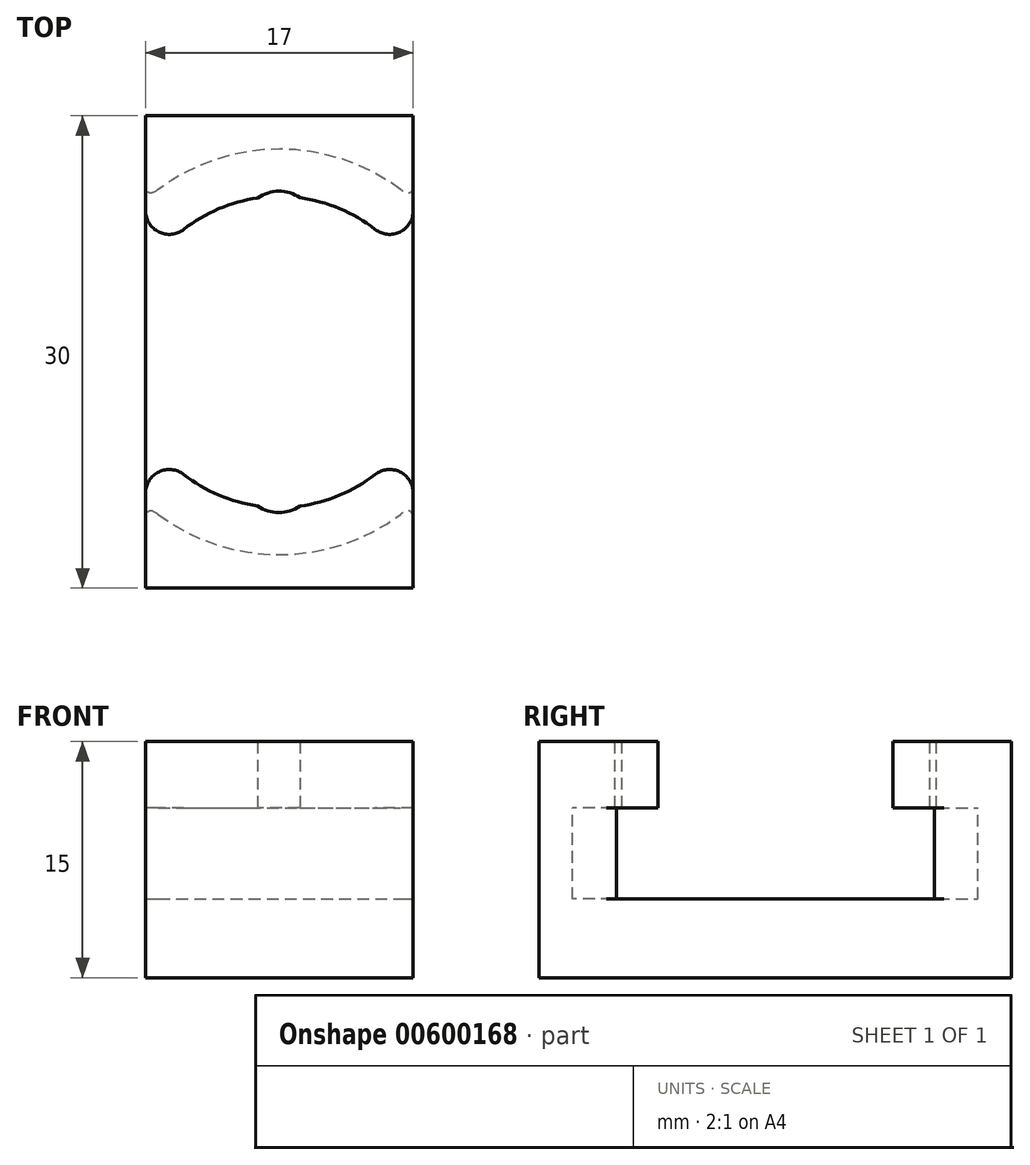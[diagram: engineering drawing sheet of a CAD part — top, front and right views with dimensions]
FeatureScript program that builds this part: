
annotation { "Feature Type Name" : "Feature", "Feature Type Description" : "" }
export const myFeature = defineFeature(function(context is Context, id is Id, definition is map)
    precondition{}
    {
        {
            var Q0;
            Q0=qCreatedBy(makeId("Top.planeOp"),FACE);
            var sketch = newSketch(context, id + "F0", { "sketchPlane" : qUnion([Q0])});
            skCircle(sketch, "E0", {"center": v(0, 0) * mm, "radius": 12.88 * mm});
            skSolve(sketch);
        }
        {
            var Q0;
            Q0=qSketchRegion(id+"F0",true);
            extrude(context, id + "F1", {"entities" : qUnion([Q0]), "oppositeDirection" : true, "depth" : 5.8 * mm, "offsetDistance" : 25 * mm});
        }
        {
            var Q0;
            Q0=qCreatedBy(makeId("Top.planeOp"),FACE);
            var sketch = newSketch(context, id + "F2", { "sketchPlane" : qUnion([Q0])});
            skCircle(sketch, "E1", {"center": v(0, 0) * mm, "radius": 9.88 * mm});
            skSolve(sketch);
        }
        {
            var Q0;
            Q0=qSketchRegion(id+"F2",true);
            extrude(context, id + "F3", {"entities" : qUnion([Q0]), "operationType" : NewBodyOperationType.ADD, "depth" : 12 * mm, "offsetDistance" : 25 * mm});
        }
        {
            var Q0;
            Q0=qCreatedBy(makeId("Top.planeOp"),FACE);
            var sketch = newSketch(context, id + "F4", { "sketchPlane" : qUnion([Q0])});
            skArc(sketch, "E2", {"start": v(1.01, 8.93) * mm, "mid": v(1, 8.94) * mm, "end": v(1, 8.95) * mm});
            skPoint(sketch, "E3.orphan", {"position": v(0, 9.05) * mm});
            skArc(sketch, "E4", {"start": v(2.13, 8.75) * mm, "mid": v(-0.03, 10.2) * mm, "end": v(-2.2, 8.75) * mm});
            skArc(sketch, "E5", {"start": v(-2.2, 8.75) * mm, "mid": v(-0.03, 9.02) * mm, "end": v(2.13, 8.76) * mm});
            skSolve(sketch);
        }
        {
            var Q0;
            Q0=qSketchRegion(id+"F4",true);
            extrude(context, id + "F5", {"entities" : qUnion([Q0]), "depth" : 5 * mm, "offsetDistance" : 25 * mm});
        }
        {
            var Q0;
            Q0=makeQuery(id+"F5.opExtrude","SWEPT_BODY",BODY,{"disambiguationData":[OSD([sQuery(id+"F4.wireOp",EDGE,"E4"),sQuery(id+"F4.wireOp",EDGE,"E5")])]});
            var Q1;
            Q1=qCreatedBy(makeId("Front.planeOp"),FACE);
            mirror(context, id + "F6", {"entities" : qUnion([Q0]), "mirrorPlane" : qUnion([Q1])});
        }
        {
            var Q0;
            Q0=qCreatedBy(makeId("Top.planeOp"),FACE);
            var sketch = newSketch(context, id + "F7", { "sketchPlane" : qUnion([Q0])});
            skLineSegment(sketch, "E6.bottom", {"start": v(-9, -13.5) * mm, "end": v(9, -13.5) * mm});
            skLineSegment(sketch, "E6.top", {"start": v(-9, 13.5) * mm, "end": v(9, 13.5) * mm});
            skLineSegment(sketch, "E6.left", {"start": v(-9, -13.5) * mm, "end": v(-9, 13.5) * mm});
            skLineSegment(sketch, "E6.right", {"start": v(9, -13.5) * mm, "end": v(9, 13.5) * mm});
            skPoint(sketch, "E6.middle", {"position": v(0, 0) * mm});
            skLineSegment(sketch, "E7.bottom", {"start": v(-15, -15) * mm, "end": v(15, -15) * mm});
            skLineSegment(sketch, "E7.top", {"start": v(-15, 15) * mm, "end": v(15, 15) * mm});
            skLineSegment(sketch, "E7.left", {"start": v(-15, -15) * mm, "end": v(-15, 15) * mm});
            skLineSegment(sketch, "E7.right", {"start": v(15, -15) * mm, "end": v(15, 15) * mm});
            skSolve(sketch);
        }
        {
            var Q0;
            Q0=qSketchRegion(id+"F7",true);
            extrude(context, id + "F8", {"entities" : qUnion([Q0]), "endBound" : BoundingType.SYMMETRIC, "depth" : 20 * mm, "offsetDistance" : 25 * mm});
        }
        {
            var Q0;
            Q0=makeQuery(id+"F8.opExtrude","SWEPT_BODY",BODY,{"disambiguationData":[OSD([sQuery(id+"F7.wireOp",EDGE,"E6.bottom"),sQuery(id+"F7.wireOp",EDGE,"E6.top"),sQuery(id+"F7.wireOp",EDGE,"E6.left"),sQuery(id+"F7.wireOp",EDGE,"E6.right"),sQuery(id+"F7.wireOp",EDGE,"E7.bottom"),sQuery(id+"F7.wireOp",EDGE,"E7.top"),sQuery(id+"F7.wireOp",EDGE,"E7.left"),sQuery(id+"F7.wireOp",EDGE,"E7.right")])]});
            var Q1;
            Q1=makeQuery(id+"F1.opExtrude","SWEPT_BODY",BODY,{"disambiguationData":[OSD([sQuery(id+"F0.wireOp",EDGE,"E0")])]});
            booleanBodies(context, id + "F9", {"operationType" : BooleanOperationType.SUBTRACTION, "tools" : qUnion([Q0]), "targets" : qUnion([Q1])});
        }
        {
            var Q0;
            Q0=qCreatedBy(makeId("Front.planeOp"),FACE);
            cPlane(context, id + "F11", {"entities" : qUnion([Q0]), "cplaneType" : CPlaneType.OFFSET, "offset" : 0 * mm, "width" : 150 * mm, "height" : 150 * mm});
        }
        {
            var Q0;
            Q0=qCreatedBy(id+"F11.planeOp",FACE);
            var sketch = newSketch(context, id + "F12", { "sketchPlane" : qUnion([Q0])});
            skLineSegment(sketch, "E8", {"start": v(0, 21.17) * mm, "end": v(0, -19.55) * mm});
            skSolve(sketch);
        }
        {
            var Q0;
            Q0=makeQuery(id+"F10.boolean.opBoolean","MERGE",FACE,{"derivedFrom":[makeQuery(id+"F1.opExtrude","CAP_FACE",FACE,{"disambiguationData":[OSD([sQuery(id+"F0.wireOp",EDGE,"E0")])],"isStart":false}),makeQuery(id+"F10.opExtrude","CAP_FACE",FACE,{"disambiguationData":[OSD([sQuery(id+"FGjzGYSQMg9Bp05_83.wireOp",EDGE,"KViSTKkF-VcMX-bRgI-X5AM-c6BNTwQ1Txp8"),sQuery(id+"FGjzGYSQMg9Bp05_83.wireOp",EDGE,"hnSNV8Ac-OkOP-zyx9-2yCD-nNF2xH7uDtxq"),sQuery(id+"FGjzGYSQMg9Bp05_83.wireOp",EDGE,"YhqCyHHE-mmT6-Zo3s-CP1x-K7R7TVIkhwK0"),sQuery(id+"FGjzGYSQMg9Bp05_83.wireOp",EDGE,"bfDPCBwk-4LN5-2Otn-u8De-q76RYstfvR2Y")])],"isStart":true})]});
            cPlane(context, id + "F14", {"entities" : qUnion([Q0]), "cplaneType" : CPlaneType.OFFSET, "offset" : 5 * mm, "width" : 150 * mm, "height" : 150 * mm});
        }
        {
            var Q0;
            Q0=qCreatedBy(id+"F14.planeOp",FACE);
            var sketch = newSketch(context, id + "F15", { "sketchPlane" : qUnion([Q0])});
            skLineSegment(sketch, "E9.bottom", {"start": v(-8.5, 15) * mm, "end": v(8.5, 15) * mm});
            skLineSegment(sketch, "E9.top", {"start": v(-8.5, -15) * mm, "end": v(8.5, -15) * mm});
            skLineSegment(sketch, "E9.left", {"start": v(-8.5, 15) * mm, "end": v(-8.5, -15) * mm});
            skLineSegment(sketch, "E9.right", {"start": v(8.5, 15) * mm, "end": v(8.5, -15) * mm});
            skPoint(sketch, "E9.middle", {"position": v(0, 0) * mm});
            skSolve(sketch);
        }
        {
            var Q0;
            Q0 = qSketchRegion(id + "F15", true);
            extrude(context, id + "F16", {"entities" : qUnion([Q0]), "oppositeDirection" : true, "depth" : 15 * mm, "offsetDistance" : 25 * mm});
        }
        {
            var Q0;
            Q0=makeQuery(id+"F13.opExtrude","SWEPT_BODY",BODY,{"disambiguationData":[OSD([sQuery(id+"FnXzy6eoX3ih6BJ_83.wireOp",EDGE,"fsWez4Eh-9LNV-7Kbs-AGMQ-t4AS18gihnjv"),sQuery(id+"FnXzy6eoX3ih6BJ_83.wireOp",EDGE,"FTZf1AKA-OWpT-rbBj-MDk0-ZM0sgJ8dLqUl"),sQuery(id+"FnXzy6eoX3ih6BJ_83.wireOp",EDGE,"cRrqmOHn-sVo0-sPzZ-KoKk-shpRNoITcmZj"),sQuery(id+"FnXzy6eoX3ih6BJ_83.wireOp",EDGE,"gythEmGH-qGAo-y04H-xNei-CAULinvqcIH7")])]});
            var Q1;
            Q1=makeQuery(id+"F6.opPattern","COPY",BODY,{"derivedFrom":makeQuery(id+"F5.opExtrude","SWEPT_BODY",BODY,{"disambiguationData":[OSD([sQuery(id+"F4.wireOp",EDGE,"E4"),sQuery(id+"F4.wireOp",EDGE,"E5")])]}),"instanceName":"1"});
            var Q2;
            Q2=makeQuery(id+"F5.opExtrude","SWEPT_BODY",BODY,{"disambiguationData":[OSD([sQuery(id+"F4.wireOp",EDGE,"E4"),sQuery(id+"F4.wireOp",EDGE,"E5")])]});
            var Q3;
            Q3=makeQuery(id+"F1.opExtrude","SWEPT_BODY",BODY,{"disambiguationData":[OSD([sQuery(id+"F0.wireOp",EDGE,"E0")])]});
            var Q4;
            Q4=makeQuery(id+"F16.opExtrude","SWEPT_BODY",BODY,{"disambiguationData":[OSD([sQuery(id+"F15.wireOp",EDGE,"E9.bottom"),sQuery(id+"F15.wireOp",EDGE,"E9.top"),sQuery(id+"F15.wireOp",EDGE,"E9.left"),sQuery(id+"F15.wireOp",EDGE,"E9.right")])]});
            booleanBodies(context, id + "F17", {"operationType" : BooleanOperationType.SUBTRACTION, "tools" : qUnion([Q0, Q1, Q2, Q3]), "targets" : qUnion([Q4])});
        }
        {
            var Q0;
            {var subQ0=sQuery(id+"F15.wireOp",EDGE,"E9.left");Q0=makeQuery(id+"FrkbQXtRzl4MnLM_85.opDeleteFace","TWEAK_EDGE",EDGE,{"derivedFrom":[makeQuery(id+"F17.opBoolean","COPY",FACE,{"disambiguationData":[TD([makeQuery(id+"F9.opBoolean","COPY",FACE,{"derivedFrom":makeQuery(id+"F8.opExtrude","SWEPT_FACE",FACE,{"disambiguationData":[OSD([sQuery(id+"F7.wireOp",EDGE,"E6.left")])]})})])],"derivedFrom":makeQuery(id+"F3.opExtrude","SWEPT_FACE",FACE,{"disambiguationData":[OSD([sQuery(id+"F2.wireOp",EDGE,"E1")])]})}),makeQuery(id+"F16.opExtrude","SWEPT_FACE",FACE,{"disambiguationData":[OSD([subQ0])]})]});}
            var Q1;
            {var subQ0=sQuery(id+"F15.wireOp",EDGE,"E9.right");Q1=makeQuery(id+"FrkbQXtRzl4MnLM_85.opDeleteFace","TWEAK_EDGE",EDGE,{"derivedFrom":[makeQuery(id+"F17.opBoolean","COPY",FACE,{"disambiguationData":[TD([makeQuery(id+"F9.opBoolean","COPY",FACE,{"derivedFrom":makeQuery(id+"F8.opExtrude","SWEPT_FACE",FACE,{"disambiguationData":[OSD([sQuery(id+"F7.wireOp",EDGE,"E6.right")])]})})])],"derivedFrom":makeQuery(id+"F3.opExtrude","SWEPT_FACE",FACE,{"disambiguationData":[OSD([sQuery(id+"F2.wireOp",EDGE,"E1")])]})}),makeQuery(id+"F16.opExtrude","SWEPT_FACE",FACE,{"disambiguationData":[OSD([subQ0])]})]});}
            var Q2;
            Q2=makeQuery(id+"F17.opBoolean","INTERSECT",EDGE,{"derivedFrom":[makeQuery(id+"F3.opExtrude","SWEPT_FACE",FACE,{"disambiguationData":[OSD([sQuery(id+"F2.wireOp",EDGE,"E1")])]}),makeQuery(id+"F16.opExtrude","SWEPT_FACE",FACE,{"disambiguationData":[OSD([sQuery(id+"F15.wireOp",EDGE,"E9.right")])]})]});
            var Q3;
            Q3=makeQuery(id+"F17.opBoolean","INTERSECT",EDGE,{"derivedFrom":[makeQuery(id+"F3.opExtrude","SWEPT_FACE",FACE,{"disambiguationData":[OSD([sQuery(id+"F2.wireOp",EDGE,"E1")])]}),makeQuery(id+"F16.opExtrude","SWEPT_FACE",FACE,{"disambiguationData":[OSD([sQuery(id+"F15.wireOp",EDGE,"E9.left")])]})]});
            fillet(context, id + "F18", {"entities" : qUnion([Q0, Q1, Q2, Q3]), "radius" : 1.5 * mm, "tangentPropagation" : true, "allowEdgeOverflow" : false});
        }
        {
            var Q0;
            Q0=makeQuery(id+"F17.opBoolean","INTERSECT",EDGE,{"derivedFrom":[makeQuery(id+"F9.opBoolean","SPLIT",FACE,{"disambiguationData":[OD(1.0)],"derivedFrom":makeQuery(id+"F1.opExtrude","SWEPT_FACE",FACE,{"disambiguationData":[OSD([sQuery(id+"F0.wireOp",EDGE,"E0")])]})}),makeQuery(id+"F16.opExtrude","SWEPT_FACE",FACE,{"disambiguationData":[OSD([sQuery(id+"F15.wireOp",EDGE,"E9.left")])]})]});
            var Q1;
            Q1=makeQuery(id+"F17.opBoolean","INTERSECT",EDGE,{"derivedFrom":[makeQuery(id+"F9.opBoolean","SPLIT",FACE,{"disambiguationData":[OD(0.0)],"derivedFrom":makeQuery(id+"F1.opExtrude","SWEPT_FACE",FACE,{"disambiguationData":[OSD([sQuery(id+"F0.wireOp",EDGE,"E0")])]})}),makeQuery(id+"F16.opExtrude","SWEPT_FACE",FACE,{"disambiguationData":[OSD([sQuery(id+"F15.wireOp",EDGE,"E9.left")])]})]});
            var Q2;
            Q2=makeQuery(id+"F17.opBoolean","INTERSECT",EDGE,{"derivedFrom":[makeQuery(id+"F9.opBoolean","SPLIT",FACE,{"disambiguationData":[OD(0.0)],"derivedFrom":makeQuery(id+"F1.opExtrude","SWEPT_FACE",FACE,{"disambiguationData":[OSD([sQuery(id+"F0.wireOp",EDGE,"E0")])]})}),makeQuery(id+"F16.opExtrude","SWEPT_FACE",FACE,{"disambiguationData":[OSD([sQuery(id+"F15.wireOp",EDGE,"E9.right")])]})]});
            var Q3;
            Q3=makeQuery(id+"F17.opBoolean","INTERSECT",EDGE,{"derivedFrom":[makeQuery(id+"F9.opBoolean","SPLIT",FACE,{"disambiguationData":[OD(1.0)],"derivedFrom":makeQuery(id+"F1.opExtrude","SWEPT_FACE",FACE,{"disambiguationData":[OSD([sQuery(id+"F0.wireOp",EDGE,"E0")])]})}),makeQuery(id+"F16.opExtrude","SWEPT_FACE",FACE,{"disambiguationData":[OSD([sQuery(id+"F15.wireOp",EDGE,"E9.right")])]})]});
            fillet(context, id + "F19", {"entities" : qUnion([Q0, Q1, Q2, Q3]), "radius" : 0.5 * mm, "tangentPropagation" : true, "rho" : 0.5, "crossSection" : FilletCrossSection.CONIC, "allowEdgeOverflow" : false});
        }
    });
